# Revit family: Hager-Vector-IP65-syst-NoHosted-PL-pl
name_source: partatom
category: Electrical Equipment
units: mm (PartAtom-declared; Revit-internal decimal feet)

## family parameters
Always vertical = Yes
Cut with Voids When Loaded = No
Panel Configuration = Two Columns, Circuits Across
Part Type = Panelboard
Room Calculation Point = No
Round Connector Dimension = Use Diameter
Shared = No
Work Plane-Based = Yes

## types (8) — shared parameters
Default Elevation = 1219 mm
EF000003 - Sposób montażu = EV000384 - Montaż natynkowy
EF000007 - Kolor = EV000270 - Szary
EF000116 - Numer RAL = 7035
EF000339 - Rodzaj pokrywy = EV004216 - Drzwi
EF001596 - Materiał obudowy = EV000139 - Tworzywo sztuczne
EF004462 - Rodzaj zamknięcia = EV000154 - Inne
EF005474 - Stopień ochrony (IP) = EV006421 - IP65
EF006244 - Transparentna pokrywa/drzwi = Yes
EF006306 - Z zamkiem = Yes
EF015776 - Listwa zaciskowa uziemienia = No
EF015777 - Listwa zaciskowa przewodu neutralnego = No
HG000001 - Liczba kolumn = 1
HG000002 - Z drzwiami lub pokrywą = Yes
HG000003 - Zakres = Vector
HG000005 - Grubość = 3 mm  [stored 0.00984252 ft]
HG000006 - Montaż podtynkowy = No
HG000009 - Drzwi dwuskrzydłowe = No
HG000010 - Drzwi asymetryczne = No
HG000011 - Puste rzędy od dołu = No
HG000017 - Odległość między biegunami = 18 mm  [stored 0.0590551 ft]
Manufacturer = Hager
Type Comments = Vector
zero-valued in all types: EF000332 - Wysokość wbudowania, EF000846 - Szerokość wbudowania, HG000007 - Liczba pustych kolumn, HG000008 - Liczba pustych rzędów

## per-type parameters (varying)
| type | EF000008 - Szerokość | EF000040 - Wysokość | EF000049 - Głębokość | EF000118 - Z płytą montażową | EF000218 - Głębokość wbudowania | EF000266 - Liczba rzędów | EF001062 - Wykonane zgodnie z Dyrektywą Kompatybilności Elektromagnetycznej EMC | EF001088 - Możliwość rozbudowy | EF001131 - Głębokość wewnętrzna | EF001134 - Szyna DIN | EF002950 - Szerokość wyrażona liczbą modułów | EF009212 - Wykonanie pokrywy | EF015941 - Drzwi przepuszczające sygnał | HG000004 - Referencja producenta | Model |
| Montaż natynkowy IP65 S250 W350 G160 10 Jednostki dywizyjne - VP20M | 250 mm  [stored 0.82021 ft] | 350 mm | 160 mm | No | 160 mm | 2 | Yes | Yes | 160 mm | Yes | 10 | EV000116 - Zamknięty | No | VP20M | VP20M |
| Montaż natynkowy IP65 S300 W300 G160 12 Jednostki dywizyjne - VP36D | 300 mm | 300 mm | 160 mm | Yes | 160 mm | 1 | No | No | 160 mm | Yes | 12 | EV009916 - Z otworem | Yes | VP36D | VP36D |
| Montaż natynkowy IP65 S300 W500 G160 12 Jednostki dywizyjne - VP36AE | 300 mm | 500 mm  [stored 1.64042 ft] | 160 mm | No | 0 mm  [stored 0 ft] | 3 | Yes | Yes | 0 mm  [stored 0 ft] | No | 12 |  | No | VP36AE | VP36AE |
| Montaż natynkowy IP65 S300 W500 G160 12 Jednostki dywizyjne - VP36M | 300 mm | 500 mm  [stored 1.64042 ft] | 160 mm | No | 160 mm | 3 | Yes | Yes | 160 mm | Yes | 12 | EV000116 - Zamknięty | No | VP36M | VP36M |
| Montaż natynkowy IP65 S400 W400 G210 18 Jednostki dywizyjne - VP54D | 400 mm  [stored 1.31234 ft] | 400 mm  [stored 1.31234 ft] | 210 mm  [stored 0.688976 ft] | Yes | 210 mm  [stored 0.688976 ft] | 1 | No | No | 210 mm  [stored 0.688976 ft] | Yes | 18 | EV009916 - Z otworem | Yes | VP54D | VP54D |
| Montaż natynkowy IP65 S400 W400 G210 18 Jednostki dywizyjne - VP72D | 400 mm  [stored 1.31234 ft] | 400 mm  [stored 1.31234 ft] | 210 mm  [stored 0.688976 ft] | Yes | 210 mm  [stored 0.688976 ft] | 1 | No | No | 210 mm  [stored 0.688976 ft] | Yes | 18 | EV009916 - Z otworem | Yes | VP72D | VP72D |
| Montaż natynkowy IP65 S400 W500 G210 18 Jednostki dywizyjne - VP54M | 400 mm  [stored 1.31234 ft] | 500 mm  [stored 1.64042 ft] | 210 mm  [stored 0.688976 ft] | No | 210 mm  [stored 0.688976 ft] | 3 | Yes | Yes | 210 mm  [stored 0.688976 ft] | Yes | 18 | EV000116 - Zamknięty | No | VP54M | VP54M |
| Montaż natynkowy IP65 S400 W650 G210 18 Jednostki dywizyjne - VP72M | 400 mm  [stored 1.31234 ft] | 650 mm  [stored 2.13255 ft] | 210 mm  [stored 0.688976 ft] | No | 210 mm  [stored 0.688976 ft] | 4 | Yes | Yes | 210 mm  [stored 0.688976 ft] | Yes | 18 | EV000116 - Zamknięty | No | VP72M | VP72M |

note: [stored X ft] marks values corroborated as IEEE doubles in the binary element streams (Revit-internal decimal feet)

## geometry (parser evidence)
native form markers: Sweep x13
no freeform markers — native parametric forms only
